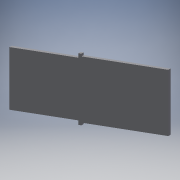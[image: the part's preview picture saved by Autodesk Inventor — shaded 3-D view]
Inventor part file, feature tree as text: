
AUTODESK INVENTOR PART (.ipt)
format: ipt  version: 2018.3 (Build 223284000, 284)  size: 3,620,352 bytes
history: native  units: mm
features: extrude x7, sketch x7, pattern_linear x2
ambient origin geometry x8: Origin, YZ Plane, XZ Plane, XY Plane, X Axis, Y Axis, Z Axis, Center Point
bodies: Body1 (feature_tree)
feature tree (16):
  extrude  "Extrusion6"  Depth=150.0mm
  extrude  "Extrusion8"  Depth=3.0mm
  extrude  "Extrusion9"  Depth=3.0mm
  extrude  "Extrusion10"  Depth=2.0mm TaperAngle=0.0deg
  extrude  "Extrusion11"  Depth=3.0mm
  extrude  "Extrusion13"  Depth=2.0mm TaperAngle=0.0deg
  extrude  "Extrusion14"  Depth=4.0mm
  pattern_linear  "Rectangular Pattern3"  Spacing1=1.0mm  [1 undecoded]
  pattern_linear  "Rectangular Pattern4"  Spacing1=2.0mm  [1 undecoded]
  sketch  "Sketch6"  dims[d18=3.0mm d19=150.0mm]
  sketch  "Sketch8"  dims[d20=120.0deg d21=3.0mm]
  sketch  "Sketch9"  dims[d22=70.0mm d23=0.0mm d27=3.0mm]
  sketch  "Sketch10"  dims[d28=5.0mm d29=0.0mm d30=2.0mm d31=0.0mm]
  sketch  "Sketch11"  dims[d32=65.0mm d33=3.0mm]
  sketch  "Sketch12"  dims[d34=5.0mm d35=0.0mm d36=2.0mm d37=0.0mm]
  sketch  "Sketch13"  dims[d38=6.0mm d39=4.0mm d40=1.0mm d41=2.0mm d50=0.6mm d51=6.0mm d52=0.6mm d53=0.5mm d54=0.5mm d55=0.0mm d56=0.4mm d57=0.0mm d58=4.0mm d59=1.0mm d60=2.0mm d61=142.0mm d62=0.5mm d63=0.0mm d64=150.0mm d66=4.6mm d67=210.0mm d69=7.0mm]
note: 2 required parameter values undecoded (feature->parameter linkage not recoverable at this tier; creation-order binding heuristic only, values carry confidence <= 0.55)
